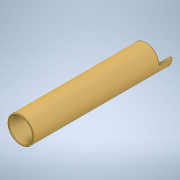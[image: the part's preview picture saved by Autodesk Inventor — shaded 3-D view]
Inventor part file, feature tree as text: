
AUTODESK INVENTOR PART (.ipt)
format: ipt  version: 2020.1 (Build 241239000, 239)  size: 179,200 bytes
history: native  units: mm
features: sketch x1
ambient origin geometry x8: Origin, YZ Plane, XZ Plane, XY Plane, X Axis, Y Axis, Z Axis, Center Point
bodies: Solid2 (feature_tree), Solid1 (feature_tree)
feature tree (1):
  sketch  "Sketch1"
